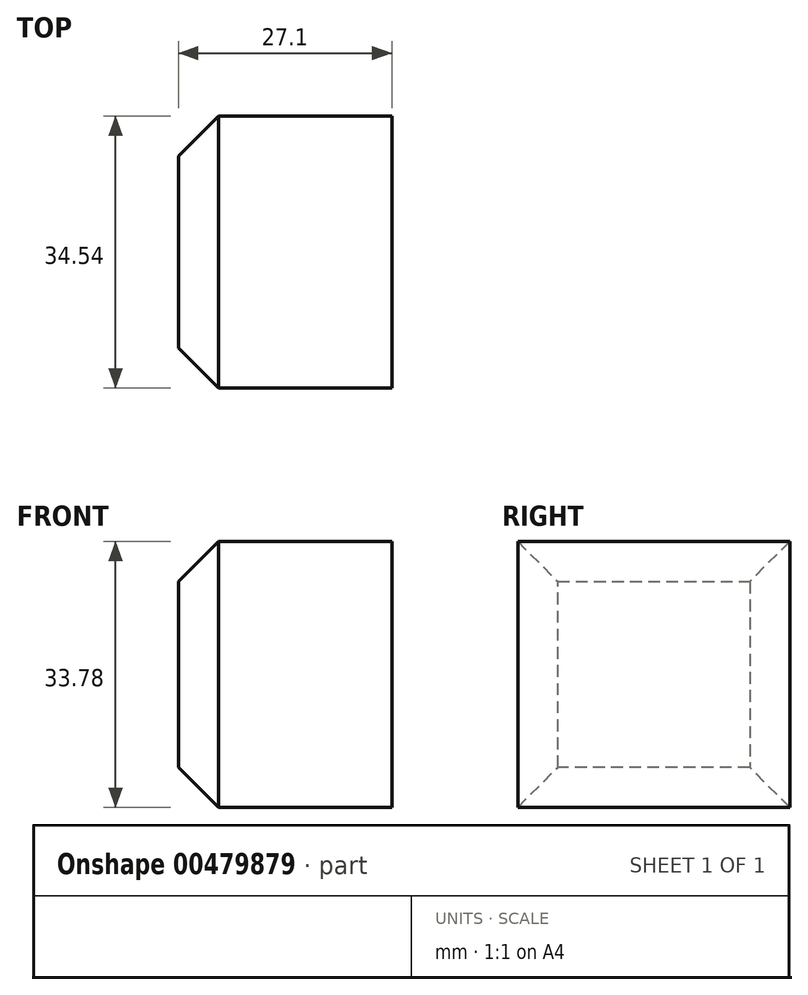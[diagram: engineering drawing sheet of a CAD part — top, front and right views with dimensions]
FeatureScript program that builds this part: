
annotation { "Feature Type Name" : "Feature", "Feature Type Description" : "" }
export const myFeature = defineFeature(function(context is Context, id is Id, definition is map)
    precondition{}
    {
        {
            var Q0;
            Q0=qCreatedBy(makeId("Front.planeOp"),FACE);
            var sketch = newSketch(context, id + "F0", { "sketchPlane" : qUnion([Q0])});
            skLineSegment(sketch, "E0.bottom", {"start": v(-50.14, -21.02) * mm, "end": v(-23.04, -21.02) * mm});
            skLineSegment(sketch, "E0.top", {"start": v(-50.14, 0) * mm, "end": v(-23.04, 0) * mm});
            skLineSegment(sketch, "E0.left", {"start": v(-50.14, -21.02) * mm, "end": v(-50.14, 0) * mm});
            skLineSegment(sketch, "E0.right", {"start": v(-23.04, -21.02) * mm, "end": v(-23.04, 0) * mm});
            skSolve(sketch);
        }
        {
            var Q0;
            Q0=sQuery(id+"F0.wireOp",EDGE,"E0.bottom");
            extrude(context, id + "F1", {"bodyType" : ToolBodyType.SURFACE, "surfaceEntities" : qUnion([Q0]), "depth" : 34.54 * mm});
        }
        {
            var Q0;
            Q0=makeQuery(id+"F1.opExtrude","SWEPT_FACE",FACE,{"disambiguationData":[OSD([sQuery(id+"F0.wireOp",EDGE,"E0.bottom")])]});
            extrude(context, id + "F2", {"entities" : qUnion([Q0]), "depth" : 33.78 * mm});
        }
        {
            var Q0;
            Q0=makeQuery(id+"F2.opExtrude","SWEPT_FACE",FACE,{"disambiguationData":[OSD([sQuery(id+"F0.wireOp",VERTEX,"E0.bottom.start")])]});
            chamfer(context, id + "F3", {"entities" : qUnion([Q0]), "width" : 5.08 * mm, "tangentPropagation" : true});
        }
    });
